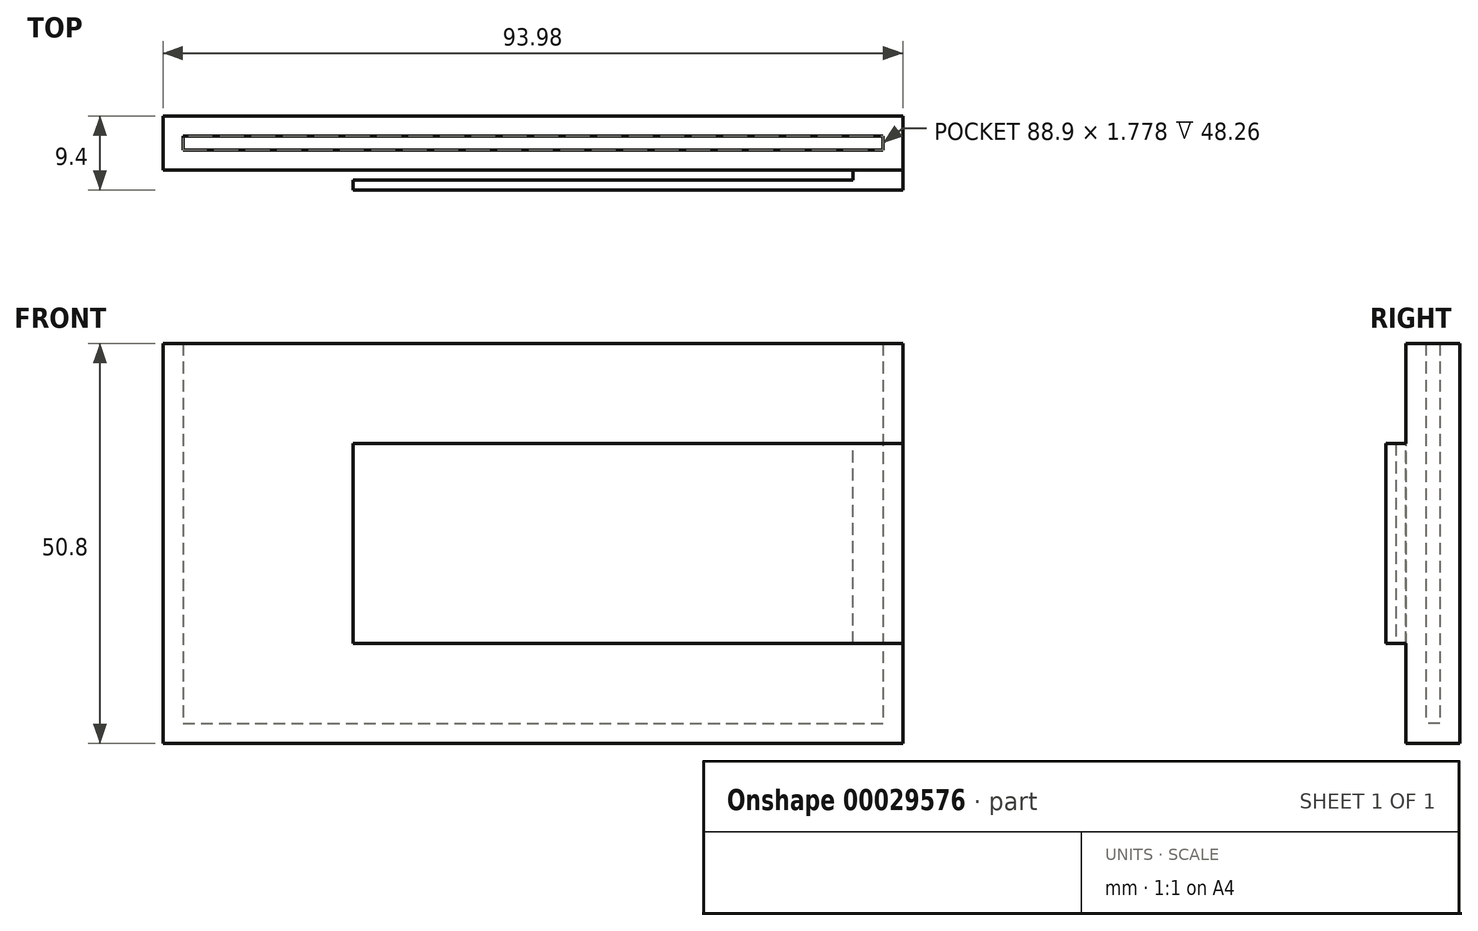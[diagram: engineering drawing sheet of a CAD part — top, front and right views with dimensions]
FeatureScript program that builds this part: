
annotation { "Feature Type Name" : "Feature", "Feature Type Description" : "" }
export const myFeature = defineFeature(function(context is Context, id is Id, definition is map)
    precondition{}
    {
        {
            var Q0;
            Q0=qCreatedBy(makeId("Top.planeOp"),FACE);
            var sketch = newSketch(context, id + "F0", { "sketchPlane" : qUnion([Q0])});
            skLineSegment(sketch, "E0.rect.bottom", {"start": v(-44.45, 0.89) * mm, "end": v(44.45, 0.89) * mm});
            skLineSegment(sketch, "E0.rect.top", {"start": v(-44.45, -0.89) * mm, "end": v(44.45, -0.89) * mm});
            skLineSegment(sketch, "E0.rect.left", {"start": v(-44.45, 0.89) * mm, "end": v(-44.45, -0.89) * mm});
            skLineSegment(sketch, "E0.rect.right", {"start": v(44.45, 0.89) * mm, "end": v(44.45, -0.89) * mm});
            skPoint(sketch, "E0.rect.middle", {"position": v(0, 0) * mm});
            skLineSegment(sketch, "E1.top", {"start": v(-44.45, 3.43) * mm, "end": v(-47, 3.43) * mm});
            skLineSegment(sketch, "E1.left", {"start": v(-44.45, -0.89) * mm, "end": v(-44.45, 3.43) * mm});
            skLineSegment(sketch, "E1.right", {"start": v(-47, -0.89) * mm, "end": v(-47, 3.43) * mm});
            skLineSegment(sketch, "E2.top", {"start": v(-47, -3.43) * mm, "end": v(-44.45, -3.43) * mm});
            skLineSegment(sketch, "E2.left", {"start": v(-47, -0.89) * mm, "end": v(-47, -3.43) * mm});
            skLineSegment(sketch, "E2.right", {"start": v(-44.45, -0.89) * mm, "end": v(-44.45, -3.43) * mm});
            skLineSegment(sketch, "E3", {"start": v(0, 0.89) * mm, "end": v(0, -0.89) * mm});
            skLineSegment(sketch, "E4.MirrorCS", {"start": v(47, -0.89) * mm, "end": v(47, -3.43) * mm});
            skLineSegment(sketch, "E5.MirrorCS", {"start": v(47, -0.89) * mm, "end": v(47, 3.43) * mm});
            skLineSegment(sketch, "E6.MirrorCS", {"start": v(44.45, 3.43) * mm, "end": v(47, 3.43) * mm});
            skLineSegment(sketch, "E7.MirrorCS", {"start": v(44.45, -0.89) * mm, "end": v(44.45, 3.43) * mm});
            skLineSegment(sketch, "E8.MirrorCS", {"start": v(44.45, -0.89) * mm, "end": v(44.45, -3.43) * mm});
            skLineSegment(sketch, "E9.MirrorCS", {"start": v(47, -3.43) * mm, "end": v(44.45, -3.43) * mm});
            skLineSegment(sketch, "E10", {"start": v(-44.45, 3.43) * mm, "end": v(44.45, 3.43) * mm});
            skLineSegment(sketch, "E11", {"start": v(-44.45, -3.43) * mm, "end": v(44.45, -3.43) * mm});
            skSolve(sketch);
        }
        {
            var Q0;
            {var subQ0=sQuery(id+"F0.wireOp",EDGE,"E3");Q0=makeQuery(id+"F0.imprint","IMPRINT",FACE,{"disambiguationData":[TD([[makeQuery(id+"F0.imprint","IMPRINT",EDGE,{"derivedFrom":subQ0}),-1.0]])]});}
            var Q1;
            {var subQ5=sQuery(id+"F0.wireOp",EDGE,"E3");Q1=makeQuery(id+"F0.imprint","IMPRINT",FACE,{"disambiguationData":[TD([[makeQuery(id+"F0.imprint","IMPRINT",EDGE,{"derivedFrom":subQ5}),1.0]])]});}
            extrude(context, id + "F1", {"entities" : qUnion([Q0, Q1]), "depth" : 2.54 * mm});
        }
        {
            var Q0;
            {var subQ0=sQuery(id+"F0.wireOp",EDGE,"E10");Q0=makeQuery(id+"F0.imprint","IMPRINT",FACE,{"disambiguationData":[TD([[makeQuery(id+"F0.imprint","IMPRINT",EDGE,{"derivedFrom":subQ0}),-1.0]])]});}
            var Q1;
            {var subQ2=sQuery(id+"F0.wireOp",EDGE,"E1.top");Q1=makeQuery(id+"F0.imprint","IMPRINT",FACE,{"disambiguationData":[TD([[makeQuery(id+"F0.imprint","IMPRINT",EDGE,{"derivedFrom":subQ2}),1.0]])]});}
            var Q2;
            {var subQ1=sQuery(id+"F0.wireOp",EDGE,"E2.right");Q2=makeQuery(id+"F0.imprint","IMPRINT",FACE,{"disambiguationData":[TD([[makeQuery(id+"F0.imprint","IMPRINT",EDGE,{"derivedFrom":subQ1}),1.0]])]});}
            var Q3;
            Q3=makeQuery(id+"F0.imprint","IMPRINT",FACE,{"disambiguationData":[TD([[makeQuery(id+"F0.imprint","IMPRINT",EDGE,{"derivedFrom":sQuery(id+"F0.wireOp",EDGE,"E4.MirrorCS")}),-1.0]])]});
            extrude(context, id + "F2", {"entities" : qUnion([Q0, Q1, Q2, Q3]), "operationType" : NewBodyOperationType.ADD, "depth" : 50.8 * mm});
        }
        {
            var Q0;
            Q0=makeQuery(id+"F2.opExtrude","SWEPT_FACE",FACE,{"disambiguationData":[OSD([sQuery(id+"F0.wireOp",EDGE,"E2.top"),sQuery(id+"F0.wireOp",EDGE,"E9.MirrorCS"),sQuery(id+"F0.wireOp",EDGE,"E11")])]});
            var sketch = newSketch(context, id + "F3", { "sketchPlane" : qUnion([Q0])});
            skLineSegment(sketch, "E12", {"start": v(47, 25.4) * mm, "end": v(-47, 25.4) * mm});
            skLineSegment(sketch, "E13", {"start": v(47, 25.4) * mm, "end": v(47, 12.7) * mm});
            skLineSegment(sketch, "E14.MirrorCS", {"start": v(46.99, 25.4) * mm, "end": v(46.99, 38.1) * mm});
            skLineSegment(sketch, "E15", {"start": v(47, 12.7) * mm, "end": v(40.7, 12.7) * mm});
            skLineSegment(sketch, "E16", {"start": v(40.7, 12.7) * mm, "end": v(40.7, 38.1) * mm});
            skLineSegment(sketch, "E17", {"start": v(46.99, 38.1) * mm, "end": v(40.7, 38.1) * mm});
            skSolve(sketch);
        }
        {
            var Q0;
            {var subQ4=sQuery(id+"F3.wireOp",EDGE,"E14.MirrorCS");Q0=makeQuery(id+"F3.imprint","IMPRINT",FACE,{"disambiguationData":[TD([[makeQuery(id+"F3.imprint","IMPRINT",EDGE,{"derivedFrom":subQ4}),-1.0]])]});}
            var Q1;
            {var subQ4=sQuery(id+"F3.wireOp",EDGE,"E13");Q1=makeQuery(id+"F3.imprint","IMPRINT",FACE,{"disambiguationData":[TD([[makeQuery(id+"F3.imprint","IMPRINT",EDGE,{"derivedFrom":subQ4}),-1.0]])]});}
            extrude(context, id + "F4", {"entities" : qUnion([Q0, Q1]), "operationType" : NewBodyOperationType.ADD, "depth" : 2.54 * mm});
        }
        {
            var Q0;
            Q0=makeQuery(id+"F4.opExtrude","SWEPT_FACE",FACE,{"disambiguationData":[OSD([sQuery(id+"F3.wireOp",EDGE,"E16")])]});
            var sketch = newSketch(context, id + "F5", { "sketchPlane" : qUnion([Q0])});
            skLineSegment(sketch, "E18.bottom", {"start": v(5.97, 38.1) * mm, "end": v(4.7, 38.1) * mm});
            skLineSegment(sketch, "E18.top", {"start": v(5.97, 12.7) * mm, "end": v(4.7, 12.7) * mm});
            skLineSegment(sketch, "E18.left", {"start": v(5.97, 38.1) * mm, "end": v(5.97, 12.7) * mm});
            skLineSegment(sketch, "E18.right", {"start": v(4.7, 38.1) * mm, "end": v(4.7, 12.7) * mm});
            skSolve(sketch);
        }
        {
            var Q0;
            Q0=makeQuery(id+"F5.imprint","IMPRINT",FACE,{"disambiguationData":[TD([[makeQuery(id+"F5.imprint","IMPRINT",EDGE,{"derivedFrom":sQuery(id+"F5.wireOp",EDGE,"E18.bottom")}),1.0]])]});
            extrude(context, id + "F6", {"entities" : qUnion([Q0]), "operationType" : NewBodyOperationType.ADD, "depth" : 63.5 * mm});
        }
    });
